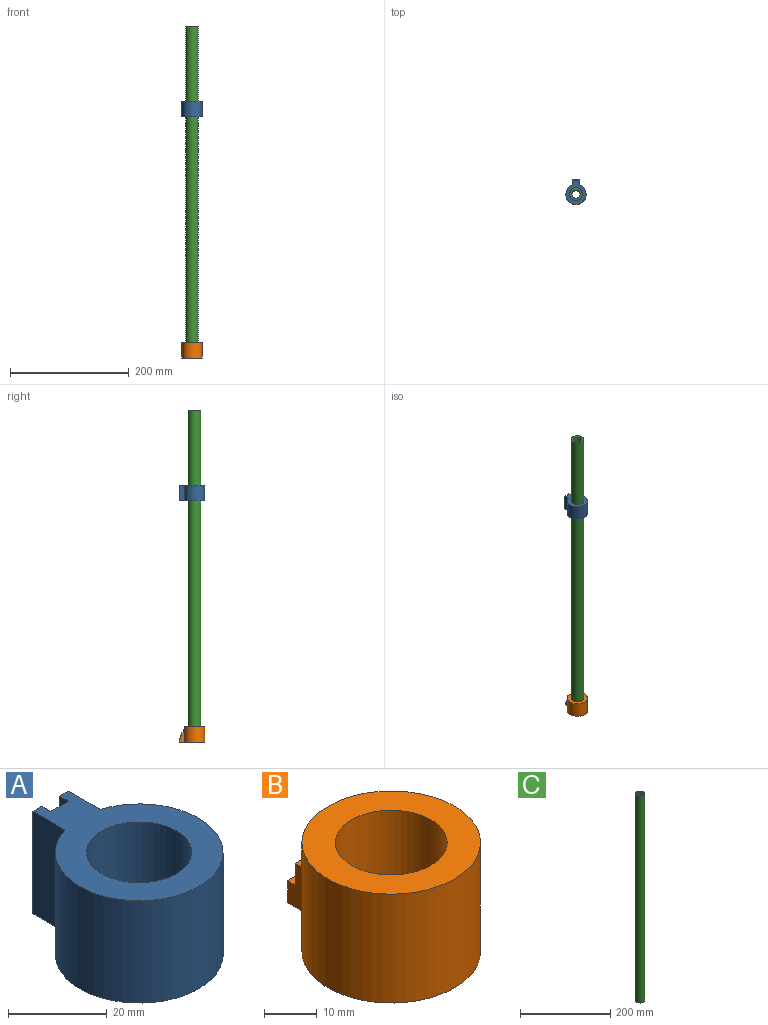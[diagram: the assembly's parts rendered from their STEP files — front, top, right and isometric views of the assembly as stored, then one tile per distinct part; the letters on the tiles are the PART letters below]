
ASSEMBLY  parts=3 mates=2
PART A: 11 faces, bbox 34x42.4x25.4 mm
  f0: plane 25.4x5.08mm, normal (0,1,0), area 129mm2, adj f1,f8,f9,f10
  f1: plane 25.4x2.54mm, normal (1,0,0), area 64.5mm2, adj f0,f2,f9,f10
  f2: plane 25.4x2.54mm, normal (0,1,0), area 64.5mm2, adj f1,f3,f9,f10
  f3: plane 25.4x9.16mm, normal (-1,0,0), area 232.6mm2, adj f2,f4,f9,f10
  f4: cylinder r=17.02mm len=34.04mm, axis (0,0,-1), area 2453.9mm2, adj f3,f5,f9,f10
  f5: plane 25.4x9.16mm, normal (1,0,0), area 232.6mm2, adj f4,f6,f9,f10
  f6: plane 25.4x2.54mm, normal (0,1,0), area 64.5mm2, adj f5,f8,f9,f10
  f7: cylinder r=10.67mm len=25.4mm, axis (0,0,-1), area 1702.5mm2, adj f9,f10
  f8: plane 25.4x2.54mm, normal (-1,0,0), area 64.5mm2, adj f0,f6,f9,f10
  f9: plane 42.42x34.04mm, normal (0,0,1), area 627.2mm2, adj f0,f1,f2,f3,f4,f5,f6,f7
  f10: plane 42.42x34.04mm, normal (0,0,-1), area 627.2mm2, adj f0,f1,f2,f3,f4,f5,f6,f7
PART B: 15 faces, bbox 34x42.4x25.4 mm
  f0: plane 20.32x8.57mm, normal (-1,0,0), area 110.3mm2, adj f3,f4,f6,f7,f8,f9,f10,f11
  f1: plane 20.32x8.57mm, normal (1,0,0), area 110.3mm2, adj f3,f4,f6,f7,f8,f9,f10,f11
  f2: plane 34.04x33.85mm, normal (0,0,1), area 551.7mm2, adj f4,f5,f14
  f3: plane 5.08x5.08mm, normal (0,1,0), area 25.8mm2, adj f0,f1,f6,f9
  f4: cylinder r=17.02mm len=34.04mm, axis (0,0,-1), area 2586.4mm2, adj f0,f1,f2,f6,f14
  f5: cylinder r=10.67mm len=25.4mm, axis (0,0,-1), area 1702.5mm2, adj f2,f6
  f6: plane 42.42x34.04mm, normal (0,0,-1), area 595.2mm2, adj f0,f1,f3,f4,f5
  f7: plane 5.08x2.1mm, normal (0,0,1), area 10.6mm2, adj f0,f1,f8,f13
  f8: plane 5.08x5.08mm, normal (0,1,0), area 25.8mm2, adj f0,f1,f7,f9
  f9: plane 5.08x2.1mm, normal (0,0,1), area 10.6mm2, adj f0,f1,f3,f8
  f10: plane 5.08x2.29mm, normal (0,0,1), area 11.6mm2, adj f0,f1,f11,f14
  f11: plane 5.08x5.08mm, normal (0,1,0), area 25.8mm2, adj f0,f1,f10,f12
  f12: plane 5.08x2.1mm, normal (0,0,1), area 10.6mm2, adj f0,f1,f11,f13
  f13: plane 5.08x5.08mm, normal (0,1,0), area 25.8mm2, adj f0,f1,f7,f12
  f14: plane 5.08x5.08mm, normal (0,1,0), area 25.8mm2, adj f2,f4,f10
PART C: 4 faces, bbox 21.3x21.3x558.8 mm
  f0: cylinder r=6.93mm len=558.8mm, axis (0,0,-1), area 24346.3mm2, adj f2,f3
  f1: cylinder r=10.67mm len=558.8mm, axis (0,0,-1), area 37455.8mm2, adj f2,f3
  f2: plane 21.34x21.34mm, normal (0,0,1), area 206.5mm2, adj f0,f1
  f3: plane 21.34x21.34mm, normal (0,0,-1), area 206.5mm2, adj f0,f1
PLACE A t=(0,0,406.4)mm
PLACE B at identity
PLACE C rot(axis=(0,0,1),90deg) t=(0,0,0)mm
MATE fastened A.f4 <-> C.f0  axis (0,0,-1) through (0,0,0)mm
MATE fastened B.f4 <-> C.f0  axis (0,0,-1) through (0,0,0)mm
